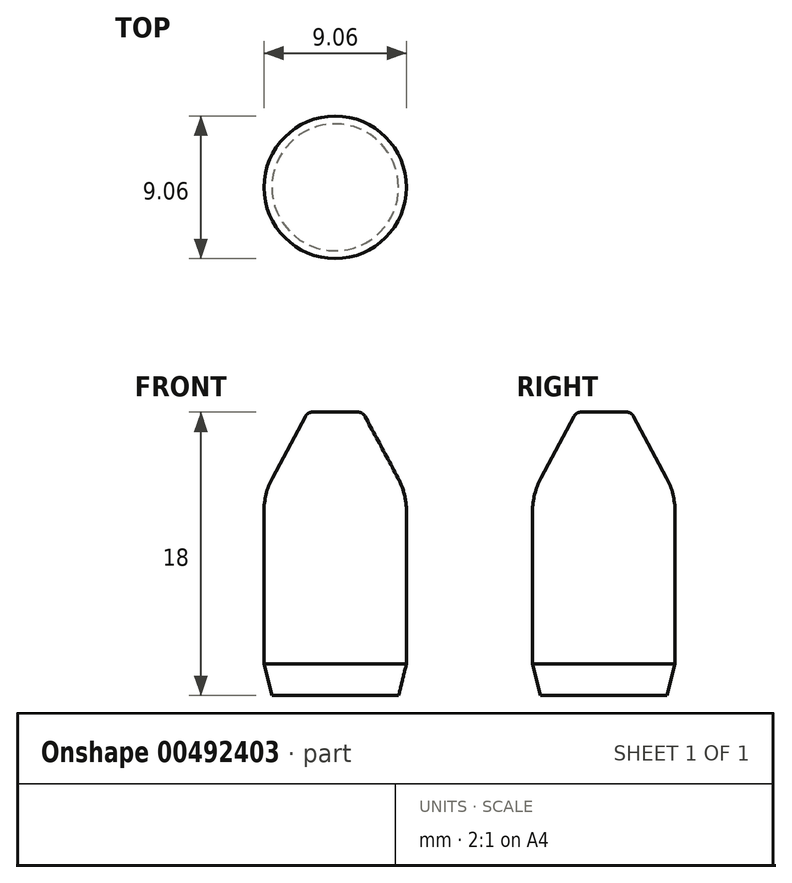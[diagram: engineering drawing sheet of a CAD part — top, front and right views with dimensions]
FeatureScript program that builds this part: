
annotation { "Feature Type Name" : "Feature", "Feature Type Description" : "" }
export const myFeature = defineFeature(function(context is Context, id is Id, definition is map)
    precondition{}
    {
        {
            var Q0;
            Q0=qCreatedBy(makeId("Front.planeOp"),FACE);
            var sketch = newSketch(context, id + "F0", { "sketchPlane" : qUnion([Q0])});
            skLineSegment(sketch, "E0", {"start": v(0, 0) * mm, "end": v(0, -14.79) * mm, "construction": true});
            skLineSegment(sketch, "E1", {"start": v(0, 0) * mm, "end": v(4.53, 0) * mm});
            skLineSegment(sketch, "E2", {"start": v(4.53, 0) * mm, "end": v(4.52, 11.68) * mm});
            skLineSegment(sketch, "E3", {"start": v(0, 18) * mm, "end": v(0, 0) * mm});
            skArc(sketch, "E4.filletArc", {"start": v(4.52, 11.68) * mm, "mid": v(4.39, 12.78) * mm, "end": v(3.99, 13.82) * mm});
            skLineSegment(sketch, "E5", {"start": v(0, 18) * mm, "end": v(1.75, 18) * mm});
            skLineSegment(sketch, "E6", {"start": v(1.75, 18) * mm, "end": v(3.99, 13.82) * mm});
            skSolve(sketch);
        }
        {
            var Q0;
            Q0=makeQuery(id+"F0.imprint","IMPRINT",FACE,{"disambiguationData":[TD([[makeQuery(id+"F0.imprint","IMPRINT",EDGE,{"derivedFrom":sQuery(id+"F0.wireOp",EDGE,"E1")}),1.0]])]});
            var Q1;
            Q1=sQuery(id+"F0.wireOp",EDGE,"E0");
            revolve(context, id + "F1", {"entities" : qUnion([Q0]), "axis" : qUnion([Q1]), "revolveType" : RevolveType.FULL});
        }
        {
            var Q0;
            Q0=makeQuery(id+"F1.opRevolve","SWEPT_EDGE",EDGE,{"disambiguationData":[OSD([sQuery(id+"F0.wireOp",EDGE,"E5"),sQuery(id+"F0.wireOp",EDGE,"E6")])]});
            fillet(context, id + "F2", {"entities" : qUnion([Q0]), "radius" : 0.5 * mm, "tangentPropagation" : true, "allowEdgeOverflow" : false});
        }
        {
            var Q0;
            Q0=makeQuery(id+"F1.opRevolve","SWEPT_EDGE",EDGE,{"disambiguationData":[OSD([sQuery(id+"F0.wireOp",EDGE,"E1"),sQuery(id+"F0.wireOp",EDGE,"E2")])]});
            chamfer(context, id + "F3", {"entities" : qUnion([Q0]), "chamferType" : ChamferType.TWO_OFFSETS, "width1" : 2 * mm, "oppositeDirection" : false, "width2" : 0.5 * mm, "tangentPropagation" : true});
        }
    });
